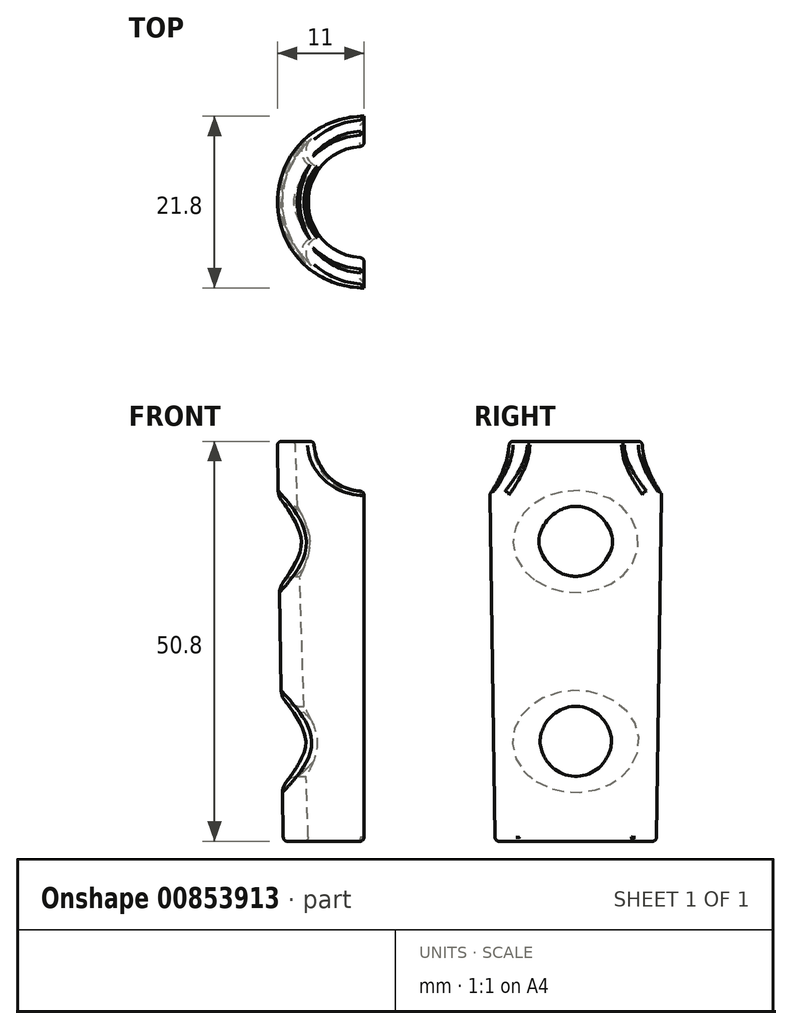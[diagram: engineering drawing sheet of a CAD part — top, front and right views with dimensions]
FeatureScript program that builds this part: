
annotation { "Feature Type Name" : "Feature", "Feature Type Description" : "" }
export const myFeature = defineFeature(function(context is Context, id is Id, definition is map)
    precondition{}
    {
        {
            var Q0;
            Q0=qCreatedBy(makeId("Top.planeOp"),FACE);
            var sketch = newSketch(context, id + "F0", { "sketchPlane" : qUnion([Q0])});
            skArc(sketch, "E0", {"start": v(0, 8.72) * mm, "mid": v(-8.72, 0) * mm, "end": v(0, -8.72) * mm});
            skArc(sketch, "E1", {"start": v(0, 11) * mm, "mid": v(-11, 0) * mm, "end": v(0, -11) * mm});
            skLineSegment(sketch, "E2", {"start": v(0, 11) * mm, "end": v(0, -11) * mm});
            skSolve(sketch);
        }
        {
            var Q0;
            Q0=qCreatedBy(makeId("Top.planeOp"),FACE);
            cPlane(context, id + "F1", {"entities" : qUnion([Q0]), "cplaneType" : CPlaneType.OFFSET, "offset" : 50.8 * mm, "oppositeDirection" : true, "width" : 152.4 * mm, "height" : 152.4 * mm});
        }
        {
            var Q0;
            Q0=qCreatedBy(id+"F1.planeOp",FACE);
            var sketch = newSketch(context, id + "F2", { "sketchPlane" : qUnion([Q0])});
            skArc(sketch, "E3", {"start": v(0, 7.07) * mm, "mid": v(-7.07, 0) * mm, "end": v(0, -7.07) * mm});
            skArc(sketch, "E4", {"start": v(0, 10.25) * mm, "mid": v(-10.25, 0) * mm, "end": v(0, -10.25) * mm});
            skLineSegment(sketch, "E5", {"start": v(0, 10.25) * mm, "end": v(0, -10.25) * mm});
            skSolve(sketch);
        }
        {
            var Q0;
            {var subQ0=sQuery(id+"F0.wireOp",EDGE,"E0");Q0=makeQuery(id+"F0.imprint","IMPRINT",FACE,{"disambiguationData":[TD([[makeQuery(id+"F0.imprint","IMPRINT",EDGE,{"derivedFrom":subQ0}),-1.0]])]});}
            var Q1;
            {var subQ0=sQuery(id+"F2.wireOp",EDGE,"E3");Q1=makeQuery(id+"F2.imprint","IMPRINT",FACE,{"disambiguationData":[TD([[makeQuery(id+"F2.imprint","IMPRINT",EDGE,{"derivedFrom":subQ0}),-1.0]])]});}
            loft(context, id + "F3", {"sheetProfilesArray" : [{ "sheetProfileEntities" : qUnion([Q0]) }, { "sheetProfileEntities" : qUnion([Q1]) }]});
        }
        {
            var Q0;
            Q0=qCreatedBy(makeId("Front.planeOp"),FACE);
            var sketch = newSketch(context, id + "F4", { "sketchPlane" : qUnion([Q0])});
            skCircle(sketch, "E6", {"center": v(0, 0) * mm, "radius": 6.35 * mm});
            skSolve(sketch);
        }
        {
            var Q0;
            Q0 = qSketchRegion(id + "F4", true);
            extrude(context, id + "F5", {"entities" : qUnion([Q0]), "operationType" : NewBodyOperationType.REMOVE, "oppositeDirection" : true, "depth" : 50.8 * mm, "offsetDistance" : 25.4 * mm, "hasSecondDirection" : true, "secondDirectionOppositeDirection" : false, "secondDirectionDepth" : 50.8 * mm});
        }
        {
            var Q0;
            Q0=qCreatedBy(makeId("Right.planeOp"),FACE);
            var sketch = newSketch(context, id + "F6", { "sketchPlane" : qUnion([Q0])});
            skLineSegment(sketch, "E7", {"start": v(0, 0) * mm, "end": v(0, -12.7) * mm, "construction": true});
            skLineSegment(sketch, "E8", {"start": v(0, -12.7) * mm, "end": v(0, -38.1) * mm, "construction": true});
            skPoint(sketch, "E8.endSnap0", {"position": v(0, -6.35) * mm});
            skCircle(sketch, "E9", {"center": v(0, -12.7) * mm, "radius": 4.45 * mm});
            skCircle(sketch, "E10", {"center": v(0, -38.1) * mm, "radius": 4.45 * mm});
            skSolve(sketch);
        }
        {
            var Q0;
            Q0 = qSketchRegion(id + "F6", true);
            extrude(context, id + "F7", {"entities" : qUnion([Q0]), "operationType" : NewBodyOperationType.REMOVE, "oppositeDirection" : true, "depth" : 50.8 * mm, "offsetDistance" : 25.4 * mm, "hasSecondDirection" : true, "secondDirectionOppositeDirection" : false, "secondDirectionDepth" : 50.8 * mm});
        }
        {
            var Q0;
            Q0=makeQuery(id+"F7.boolean.opBoolean","INTERSECT",EDGE,{"derivedFrom":[makeQuery(id+"F3.opLoft","SWEPT_FACE",FACE,{"disambiguationData":[OSD([sQuery(id+"F0.wireOp",EDGE,"E1"),sQuery(id+"F0.wireOp",EDGE,"E2"),sQuery(id+"F2.wireOp",EDGE,"E4"),sQuery(id+"F2.wireOp",EDGE,"E5")])]}),makeQuery(id+"F7.opExtrude","SWEPT_FACE",FACE,{"disambiguationData":[OSD([sQuery(id+"F6.wireOp",EDGE,"E10")])]})]});
            var Q1;
            Q1=makeQuery(id+"F7.boolean.opBoolean","INTERSECT",EDGE,{"derivedFrom":[makeQuery(id+"F3.opLoft","SWEPT_FACE",FACE,{"disambiguationData":[OSD([sQuery(id+"F0.wireOp",EDGE,"E1"),sQuery(id+"F0.wireOp",EDGE,"E2"),sQuery(id+"F2.wireOp",EDGE,"E4"),sQuery(id+"F2.wireOp",EDGE,"E5")])]}),makeQuery(id+"F7.opExtrude","SWEPT_FACE",FACE,{"disambiguationData":[OSD([sQuery(id+"F6.wireOp",EDGE,"E9")])]})]});
            fillet(context, id + "F8", {"entities" : qUnion([Q0, Q1]), "radius" : 2.03 * mm, "tangentPropagation" : true, "allowEdgeOverflow" : false});
        }
        {
            var Q0;
            Q0=makeQuery(id+"F5.boolean.opBoolean","INTERSECT",EDGE,{"disambiguationData":[OD(1.0)],"derivedFrom":[makeQuery(id+"F3.opLoft","SWEPT_FACE",FACE,{"disambiguationData":[OSD([sQuery(id+"F0.wireOp",EDGE,"E0"),sQuery(id+"F0.wireOp",EDGE,"E2"),sQuery(id+"F2.wireOp",EDGE,"E3"),sQuery(id+"F2.wireOp",EDGE,"E5")])]}),makeQuery(id+"F5.opExtrude","SWEPT_FACE",FACE,{"disambiguationData":[OSD([sQuery(id+"F4.wireOp",EDGE,"E6")])]})]});
            var Q1;
            Q1=makeQuery(id+"F5.boolean.opBoolean","INTERSECT",EDGE,{"disambiguationData":[OD(0.0)],"derivedFrom":[makeQuery(id+"F3.opLoft","SWEPT_FACE",FACE,{"disambiguationData":[OSD([sQuery(id+"F0.wireOp",EDGE,"E0"),sQuery(id+"F0.wireOp",EDGE,"E2"),sQuery(id+"F2.wireOp",EDGE,"E3"),sQuery(id+"F2.wireOp",EDGE,"E5")])]}),makeQuery(id+"F5.opExtrude","SWEPT_FACE",FACE,{"disambiguationData":[OSD([sQuery(id+"F4.wireOp",EDGE,"E6")])]})]});
            var Q2;
            Q2=makeQuery(id+"F3.opLoft","MID_CAP_EDGE",EDGE,{"disambiguationData":[OSD([sQuery(id+"F0.wireOp",EDGE,"E0"),sQuery(id+"F0.wireOp",EDGE,"E2")])],"capPos":0.0});
            var Q3;
            {var subQ0=sQuery(id+"F0.wireOp",EDGE,"E0");Q3=makeQuery(id+"F5.boolean.opBoolean","INTERSECT",EDGE,{"disambiguationData":[OD(1.0)],"derivedFrom":[makeQuery(id+"F3.opLoft","CAP_FACE",FACE,{"disambiguationData":[OSD([makeQuery(id+"F0.imprint","IMPRINT",FACE,{"disambiguationData":[TD([[makeQuery(id+"F0.imprint","IMPRINT",EDGE,{"derivedFrom":subQ0}),-1.0]])]})])],"isStart":true}),makeQuery(id+"F5.opExtrude","SWEPT_FACE",FACE,{"disambiguationData":[OSD([sQuery(id+"F4.wireOp",EDGE,"E6")])]})]});}
            var Q4;
            {var subQ0=sQuery(id+"F0.wireOp",EDGE,"E0");Q4=makeQuery(id+"F5.boolean.opBoolean","INTERSECT",EDGE,{"disambiguationData":[OD(0.0)],"derivedFrom":[makeQuery(id+"F3.opLoft","CAP_FACE",FACE,{"disambiguationData":[OSD([makeQuery(id+"F0.imprint","IMPRINT",FACE,{"disambiguationData":[TD([[makeQuery(id+"F0.imprint","IMPRINT",EDGE,{"derivedFrom":subQ0}),-1.0]])]})])],"isStart":true}),makeQuery(id+"F5.opExtrude","SWEPT_FACE",FACE,{"disambiguationData":[OSD([sQuery(id+"F4.wireOp",EDGE,"E6")])]})]});}
            var Q5;
            Q5=makeQuery(id+"F5.boolean.opBoolean","INTERSECT",EDGE,{"disambiguationData":[OD(1.0)],"derivedFrom":[makeQuery(id+"F3.opLoft","SWEPT_FACE",FACE,{"disambiguationData":[OSD([sQuery(id+"F0.wireOp",EDGE,"E1"),sQuery(id+"F0.wireOp",EDGE,"E2"),sQuery(id+"F2.wireOp",EDGE,"E4"),sQuery(id+"F2.wireOp",EDGE,"E5")])]}),makeQuery(id+"F5.opExtrude","SWEPT_FACE",FACE,{"disambiguationData":[OSD([sQuery(id+"F4.wireOp",EDGE,"E6")])]})]});
            var Q6;
            Q6=makeQuery(id+"F5.boolean.opBoolean","INTERSECT",EDGE,{"disambiguationData":[OD(0.0)],"derivedFrom":[makeQuery(id+"F3.opLoft","SWEPT_FACE",FACE,{"disambiguationData":[OSD([sQuery(id+"F0.wireOp",EDGE,"E1"),sQuery(id+"F0.wireOp",EDGE,"E2"),sQuery(id+"F2.wireOp",EDGE,"E4"),sQuery(id+"F2.wireOp",EDGE,"E5")])]}),makeQuery(id+"F5.opExtrude","SWEPT_FACE",FACE,{"disambiguationData":[OSD([sQuery(id+"F4.wireOp",EDGE,"E6")])]})]});
            var Q7;
            Q7=makeQuery(id+"F3.opLoft","MID_CAP_EDGE",EDGE,{"disambiguationData":[OSD([sQuery(id+"F0.wireOp",EDGE,"E1"),sQuery(id+"F0.wireOp",EDGE,"E2")])],"capPos":0.0});
            var Q8;
            {var subQ0=sQuery(id+"F2.wireOp",EDGE,"E5");var subQ1=sQuery(id+"F2.wireOp",EDGE,"E3");var subQ2=makeQuery(id+"F2.imprint","INTERSECT",VERTEX,{"disambiguationData":[OD(1.0)],"derivedFrom":[subQ1,subQ0]});var subQ3=sQuery(id+"F2.wireOp",EDGE,"E4");var subQ4=makeQuery(id+"F2.imprint","INTERSECT",VERTEX,{"disambiguationData":[OD(1.0)],"derivedFrom":[subQ3,subQ0]});var subQ5=sQuery(id+"F0.wireOp",EDGE,"E2");var subQ6=sQuery(id+"F0.wireOp",EDGE,"E0");var subQ7=makeQuery(id+"F0.imprint","INTERSECT",VERTEX,{"disambiguationData":[OD(1.0)],"derivedFrom":[subQ6,subQ5]});var subQ8=sQuery(id+"F0.wireOp",EDGE,"E1");var subQ9=makeQuery(id+"F0.imprint","INTERSECT",VERTEX,{"disambiguationData":[OD(1.0)],"derivedFrom":[subQ8,subQ5]});Q8=makeQuery(id+"F5.boolean.opBoolean","INTERSECT",EDGE,{"derivedFrom":[makeQuery(id+"F3.opLoft","SWEPT_FACE",FACE,{"disambiguationData":[OSD([subQ6,subQ8,subQ5,subQ1,subQ3,subQ0]),TDD([subQ7,subQ9,makeQuery(id+"F0.imprint","IMPRINT",EDGE,{"disambiguationData":[TD([[subQ7,-1.0]])],"derivedFrom":subQ5}),subQ2,subQ4,makeQuery(id+"F2.imprint","IMPRINT",EDGE,{"disambiguationData":[TD([[subQ2,-1.0]])],"derivedFrom":subQ0})])]}),makeQuery(id+"F5.opExtrude","SWEPT_FACE",FACE,{"disambiguationData":[OSD([sQuery(id+"F4.wireOp",EDGE,"E6")])]})]});}
            var Q9;
            {var subQ0=sQuery(id+"F2.wireOp",EDGE,"E5");var subQ1=sQuery(id+"F2.wireOp",EDGE,"E3");var subQ2=makeQuery(id+"F2.imprint","INTERSECT",VERTEX,{"disambiguationData":[OD(0.0)],"derivedFrom":[subQ1,subQ0]});var subQ3=sQuery(id+"F2.wireOp",EDGE,"E4");var subQ4=makeQuery(id+"F2.imprint","INTERSECT",VERTEX,{"disambiguationData":[OD(0.0)],"derivedFrom":[subQ3,subQ0]});var subQ5=sQuery(id+"F0.wireOp",EDGE,"E2");var subQ6=sQuery(id+"F0.wireOp",EDGE,"E0");var subQ7=makeQuery(id+"F0.imprint","INTERSECT",VERTEX,{"disambiguationData":[OD(0.0)],"derivedFrom":[subQ6,subQ5]});var subQ8=sQuery(id+"F0.wireOp",EDGE,"E1");var subQ9=makeQuery(id+"F0.imprint","INTERSECT",VERTEX,{"disambiguationData":[OD(0.0)],"derivedFrom":[subQ8,subQ5]});Q9=makeQuery(id+"F5.boolean.opBoolean","INTERSECT",EDGE,{"derivedFrom":[makeQuery(id+"F3.opLoft","SWEPT_FACE",FACE,{"disambiguationData":[OSD([subQ6,subQ8,subQ5,subQ1,subQ3,subQ0]),TDD([subQ7,subQ9,makeQuery(id+"F0.imprint","IMPRINT",EDGE,{"disambiguationData":[TD([[subQ7,1.0]])],"derivedFrom":subQ5}),subQ2,subQ4,makeQuery(id+"F2.imprint","IMPRINT",EDGE,{"disambiguationData":[TD([[subQ2,1.0]])],"derivedFrom":subQ0})])]}),makeQuery(id+"F5.opExtrude","SWEPT_FACE",FACE,{"disambiguationData":[OSD([sQuery(id+"F4.wireOp",EDGE,"E6")])]})]});}
            var Q10;
            {var subQ0=sQuery(id+"F2.wireOp",EDGE,"E5");var subQ1=sQuery(id+"F2.wireOp",EDGE,"E3");var subQ2=makeQuery(id+"F2.imprint","INTERSECT",VERTEX,{"disambiguationData":[OD(1.0)],"derivedFrom":[subQ1,subQ0]});var subQ3=sQuery(id+"F2.wireOp",EDGE,"E4");var subQ4=makeQuery(id+"F2.imprint","INTERSECT",VERTEX,{"disambiguationData":[OD(1.0)],"derivedFrom":[subQ3,subQ0]});Q10=makeQuery(id+"F3.opLoft","MID_CAP_EDGE",EDGE,{"disambiguationData":[OSD([subQ1,subQ3,subQ0]),TDD([subQ2,subQ4,makeQuery(id+"F2.imprint","IMPRINT",EDGE,{"disambiguationData":[TD([[subQ2,-1.0]])],"derivedFrom":subQ0})])],"capPos":1.0});}
            var Q11;
            {var subQ0=sQuery(id+"F2.wireOp",EDGE,"E5");var subQ1=sQuery(id+"F2.wireOp",EDGE,"E3");var subQ2=makeQuery(id+"F2.imprint","INTERSECT",VERTEX,{"disambiguationData":[OD(0.0)],"derivedFrom":[subQ1,subQ0]});var subQ3=sQuery(id+"F2.wireOp",EDGE,"E4");var subQ4=makeQuery(id+"F2.imprint","INTERSECT",VERTEX,{"disambiguationData":[OD(0.0)],"derivedFrom":[subQ3,subQ0]});Q11=makeQuery(id+"F3.opLoft","MID_CAP_EDGE",EDGE,{"disambiguationData":[OSD([subQ1,subQ3,subQ0]),TDD([subQ2,subQ4,makeQuery(id+"F2.imprint","IMPRINT",EDGE,{"disambiguationData":[TD([[subQ2,1.0]])],"derivedFrom":subQ0})])],"capPos":1.0});}
            var Q12;
            Q12=makeQuery(id+"F3.opLoft","MID_CAP_EDGE",EDGE,{"disambiguationData":[OSD([sQuery(id+"F2.wireOp",EDGE,"E3"),sQuery(id+"F2.wireOp",EDGE,"E5")])],"capPos":1.0});
            var Q13;
            Q13=makeQuery(id+"F3.opLoft","MID_CAP_EDGE",EDGE,{"disambiguationData":[OSD([sQuery(id+"F2.wireOp",EDGE,"E4"),sQuery(id+"F2.wireOp",EDGE,"E5")])],"capPos":1.0});
            var Q14;
            {var subQ0=sQuery(id+"F2.wireOp",EDGE,"E5");var subQ1=sQuery(id+"F2.wireOp",EDGE,"E3");var subQ2=sQuery(id+"F0.wireOp",EDGE,"E2");var subQ3=sQuery(id+"F0.wireOp",EDGE,"E0");Q14=makeQuery(id+"F3.opLoft","SWEPT_EDGE",EDGE,{"disambiguationData":[OSD([subQ3,subQ2,subQ1,subQ0]),TDD([makeQuery(id+"F0.imprint","INTERSECT",VERTEX,{"disambiguationData":[OD(1.0)],"derivedFrom":[subQ3,subQ2]}),makeQuery(id+"F2.imprint","INTERSECT",VERTEX,{"disambiguationData":[OD(1.0)],"derivedFrom":[subQ1,subQ0]})])]});}
            var Q15;
            {var subQ0=sQuery(id+"F2.wireOp",EDGE,"E5");var subQ1=sQuery(id+"F2.wireOp",EDGE,"E3");var subQ2=sQuery(id+"F0.wireOp",EDGE,"E2");var subQ3=sQuery(id+"F0.wireOp",EDGE,"E0");Q15=makeQuery(id+"F3.opLoft","SWEPT_EDGE",EDGE,{"disambiguationData":[OSD([subQ3,subQ2,subQ1,subQ0]),TDD([makeQuery(id+"F0.imprint","INTERSECT",VERTEX,{"disambiguationData":[OD(0.0)],"derivedFrom":[subQ3,subQ2]}),makeQuery(id+"F2.imprint","INTERSECT",VERTEX,{"disambiguationData":[OD(0.0)],"derivedFrom":[subQ1,subQ0]})])]});}
            fillet(context, id + "F9", {"entities" : qUnion([Q0, Q1, Q2, Q3, Q4, Q5, Q6, Q7, Q8, Q9, Q10, Q11, Q12, Q13, Q14, Q15]), "radius" : 0.5 * mm, "tangentPropagation" : true, "allowEdgeOverflow" : false});
        }
    });
